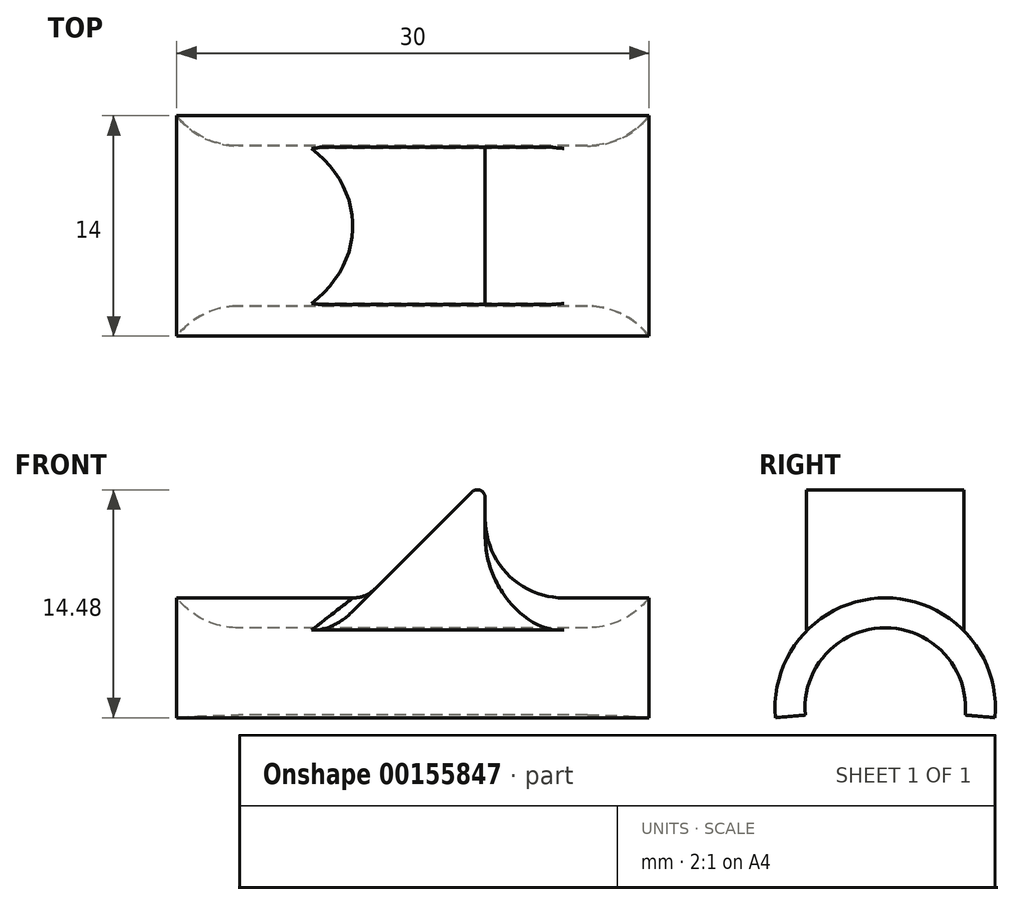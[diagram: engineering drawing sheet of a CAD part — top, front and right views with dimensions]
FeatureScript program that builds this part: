
annotation { "Feature Type Name" : "Feature", "Feature Type Description" : "" }
export const myFeature = defineFeature(function(context is Context, id is Id, definition is map)
    precondition{}
    {
        {
            var Q0;
            Q0=qCreatedBy(makeId("Front.planeOp"),FACE);
            var sketch = newSketch(context, id + "F0", { "sketchPlane" : qUnion([Q0])});
            skLineSegment(sketch, "E0.top", {"start": v(4.6, 4.97) * mm, "end": v(-5.01, 4.97) * mm});
            skLineSegment(sketch, "E0.left", {"start": v(4.6, 14.57) * mm, "end": v(4.6, 4.97) * mm});
            skLineSegment(sketch, "E1", {"start": v(4.6, 14.57) * mm, "end": v(-5.01, 4.97) * mm});
            skSolve(sketch);
        }
        {
            var Q0;
            Q0=qCreatedBy(makeId("Right.planeOp"),FACE);
            var sketch = newSketch(context, id + "F1", { "sketchPlane" : qUnion([Q0])});
            skArc(sketch, "E2", {"start": v(5.08, -0.44) * mm, "mid": v(0, 5.1) * mm, "end": v(-5.08, -0.44) * mm});
            skArc(sketch, "E3", {"start": v(6.97, -0.61) * mm, "mid": v(0, 7) * mm, "end": v(-6.97, -0.61) * mm});
            skLineSegment(sketch, "E4", {"start": v(0, 0) * mm, "end": v(-19.92, -1.74) * mm, "construction": true});
            skLineSegment(sketch, "E5", {"start": v(0, 0) * mm, "end": v(19.92, -1.74) * mm, "construction": true});
            skLineSegment(sketch, "E6", {"start": v(5.08, -0.44) * mm, "end": v(6.97, -0.61) * mm});
            skLineSegment(sketch, "E7", {"start": v(-6.97, -0.61) * mm, "end": v(-5.08, -0.44) * mm});
            skSolve(sketch);
        }
        {
            var Q0;
            Q0=makeQuery(id+"F1.imprint","IMPRINT",FACE,{"disambiguationData":[TD([[makeQuery(id+"F1.imprint","IMPRINT",EDGE,{"derivedFrom":sQuery(id+"F1.wireOp",EDGE,"E2")}),-1.0]])]});
            extrude(context, id + "F2", {"entities" : qUnion([Q0]), "endBound" : BoundingType.SYMMETRIC, "depth" : 30 * mm});
        }
        {
            var Q0;
            Q0=makeQuery(id+"F0.imprint","IMPRINT",FACE,{"disambiguationData":[TD([[makeQuery(id+"F0.imprint","IMPRINT",EDGE,{"derivedFrom":sQuery(id+"F0.wireOp",EDGE,"E0.top")}),-1.0]])]});
            extrude(context, id + "F3", {"entities" : qUnion([Q0]), "operationType" : NewBodyOperationType.ADD, "endBound" : BoundingType.SYMMETRIC, "depth" : 10 * mm});
        }
        {
            var Q0;
            Q0=makeQuery(id+"F3.boolean.opBoolean","INTERSECT",EDGE,{"derivedFrom":[makeQuery(id+"F2.opExtrude","SWEPT_FACE",FACE,{"disambiguationData":[OSD([sQuery(id+"F1.wireOp",EDGE,"E3")])]}),makeQuery(id+"F3.opExtrude","SWEPT_FACE",FACE,{"disambiguationData":[OSD([sQuery(id+"F0.wireOp",EDGE,"E0.left")])]})]});
            fillet(context, id + "F4", {"entities" : qUnion([Q0]), "radius" : 5 * mm, "tangentPropagation" : true, "allowEdgeOverflow" : false});
        }
        {
            var Q0;
            Q0=qCreatedBy(makeId("Right.planeOp"),FACE);
            var sketch = newSketch(context, id + "F5", { "sketchPlane" : qUnion([Q0])});
            skCircle(sketch, "E8", {"center": v(0, 0) * mm, "radius": 5.1 * mm});
            skSolve(sketch);
        }
        {
            var Q0;
            Q0=makeQuery(id+"F5.imprint","IMPRINT",FACE,{"disambiguationData":[TD([[makeQuery(id+"F5.imprint","IMPRINT",EDGE,{"derivedFrom":sQuery(id+"F5.wireOp",EDGE,"E8")}),1.0]])]});
            extrude(context, id + "F6", {"entities" : qUnion([Q0]), "operationType" : NewBodyOperationType.REMOVE, "endBound" : BoundingType.SYMMETRIC, "depth" : 25 * mm});
        }
        {
            var Q0;
            Q0=makeQuery(id+"F2.opExtrude","CAP_EDGE",EDGE,{"disambiguationData":[OSD([sQuery(id+"F1.wireOp",EDGE,"E2")])],"isStart":true});
            var Q1;
            Q1=makeQuery(id+"F2.opExtrude","CAP_EDGE",EDGE,{"disambiguationData":[OSD([sQuery(id+"F1.wireOp",EDGE,"E2")])],"isStart":false});
            fillet(context, id + "F7", {"entities" : qUnion([Q0, Q1]), "radius" : 5 * mm, "tangentPropagation" : true, "allowEdgeOverflow" : false});
        }
        {
            var Q0;
            Q0=makeQuery(id+"F3.opExtrude","SWEPT_EDGE",EDGE,{"disambiguationData":[OSD([sQuery(id+"F0.wireOp",EDGE,"E0.left"),sQuery(id+"F0.wireOp",EDGE,"E1")])]});
            fillet(context, id + "F8", {"entities" : qUnion([Q0]), "radius" : 0.5 * mm, "tangentPropagation" : true, "allowEdgeOverflow" : false});
        }
        {
            var Q0;
            Q0=makeQuery(id+"F3.boolean.opBoolean","INTERSECT",EDGE,{"derivedFrom":[makeQuery(id+"F2.opExtrude","SWEPT_FACE",FACE,{"disambiguationData":[OSD([sQuery(id+"F1.wireOp",EDGE,"E3")])]}),makeQuery(id+"F3.opExtrude","SWEPT_FACE",FACE,{"disambiguationData":[OSD([sQuery(id+"F0.wireOp",EDGE,"E1")])]})]});
            fillet(context, id + "F9", {"entities" : qUnion([Q0]), "radius" : 2 * mm, "tangentPropagation" : true, "allowEdgeOverflow" : false});
        }
    });
